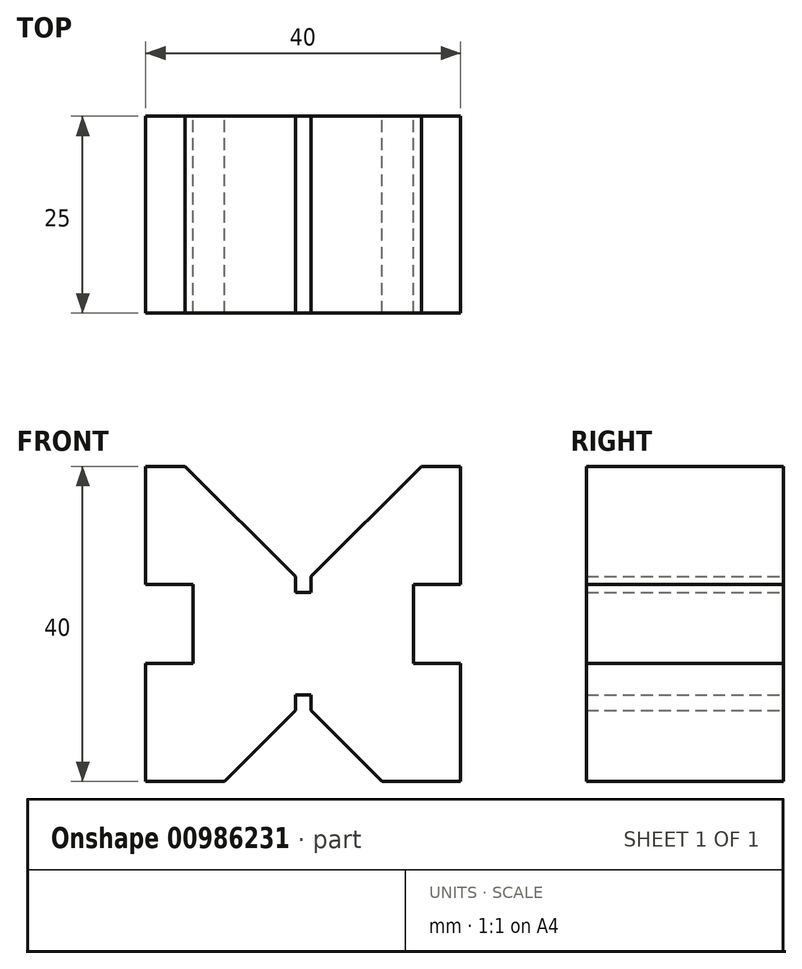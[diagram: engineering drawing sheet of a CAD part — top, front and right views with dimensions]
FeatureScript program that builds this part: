
annotation { "Feature Type Name" : "Feature", "Feature Type Description" : "" }
export const myFeature = defineFeature(function(context is Context, id is Id, definition is map)
    precondition{}
    {
        {
            var Q0;
            Q0=qCreatedBy(makeId("Front.planeOp"),FACE);
            var sketch = newSketch(context, id + "F0", { "sketchPlane" : qUnion([Q0])});
            skLineSegment(sketch, "E0.bottom", {"start": v(0, 0) * mm, "end": v(40, 0) * mm});
            skLineSegment(sketch, "E0.top", {"start": v(0, 40) * mm, "end": v(5, 40) * mm});
            skLineSegment(sketch, "E0.left", {"start": v(0, 0) * mm, "end": v(0, 15) * mm});
            skLineSegment(sketch, "E0.right", {"start": v(40, 0) * mm, "end": v(40, 15) * mm});
            skLineSegment(sketch, "E1", {"start": v(0, 15) * mm, "end": v(6, 15) * mm});
            skLineSegment(sketch, "E2", {"start": v(6, 15) * mm, "end": v(6, 25) * mm});
            skLineSegment(sketch, "E3", {"start": v(6, 25) * mm, "end": v(0, 25) * mm});
            skLineSegment(sketch, "E4", {"start": v(5, 40) * mm, "end": v(19, 26) * mm});
            skLineSegment(sketch, "E5", {"start": v(19, 26) * mm, "end": v(19, 24) * mm});
            skLineSegment(sketch, "E6", {"start": v(19, 24) * mm, "end": v(21, 24) * mm});
            skLineSegment(sketch, "E7", {"start": v(21, 24) * mm, "end": v(21, 26) * mm});
            skLineSegment(sketch, "E8", {"start": v(21, 26) * mm, "end": v(35, 40) * mm});
            skLineSegment(sketch, "E9.trimOffspring", {"start": v(0, 25) * mm, "end": v(0, 40) * mm});
            skLineSegment(sketch, "E10", {"start": v(34, 25) * mm, "end": v(40, 25) * mm});
            skLineSegment(sketch, "E11", {"start": v(34, 25) * mm, "end": v(34, 15) * mm});
            skLineSegment(sketch, "E12", {"start": v(34, 15) * mm, "end": v(40, 15) * mm});
            skLineSegment(sketch, "E13", {"start": v(20, 40) * mm, "end": v(20, 0) * mm, "construction": true});
            skLineSegment(sketch, "E14.trimOffspring", {"start": v(40, 25) * mm, "end": v(40, 40) * mm});
            skLineSegment(sketch, "E15", {"start": v(19, 11) * mm, "end": v(21, 11) * mm});
            skCircle(sketch, "E16", {"center": v(2.23, 1.75) * mm, "radius": 1.03 * mm, "construction": true});
            skLineSegment(sketch, "E17", {"start": v(19, 11) * mm, "end": v(19, 9) * mm});
            skLineSegment(sketch, "E18", {"start": v(19, 9) * mm, "end": v(10, 0) * mm});
            skPoint(sketch, "E19.end.orphan", {"position": v(30, 0) * mm});
            skLineSegment(sketch, "E20", {"start": v(21, 11) * mm, "end": v(21, 9) * mm});
            skLineSegment(sketch, "E21", {"start": v(21, 9) * mm, "end": v(30, 0) * mm});
            skLineSegment(sketch, "E22.trimOffspring", {"start": v(35, 40) * mm, "end": v(40, 40) * mm});
            skSolve(sketch);
        }
        {
            var Q0;
            Q0=makeQuery(id+"F0.imprint","IMPRINT",FACE,{"disambiguationData":[TD([[makeQuery(id+"F0.imprint","IMPRINT",EDGE,{"derivedFrom":sQuery(id+"F0.wireOp",EDGE,"E0.top")}),-1.0]])]});
            extrude(context, id + "F1", {"entities" : qUnion([Q0]), "endBound" : BoundingType.SYMMETRIC, "depth" : 25 * mm, "offsetDistance" : 25 * mm});
        }
    });
